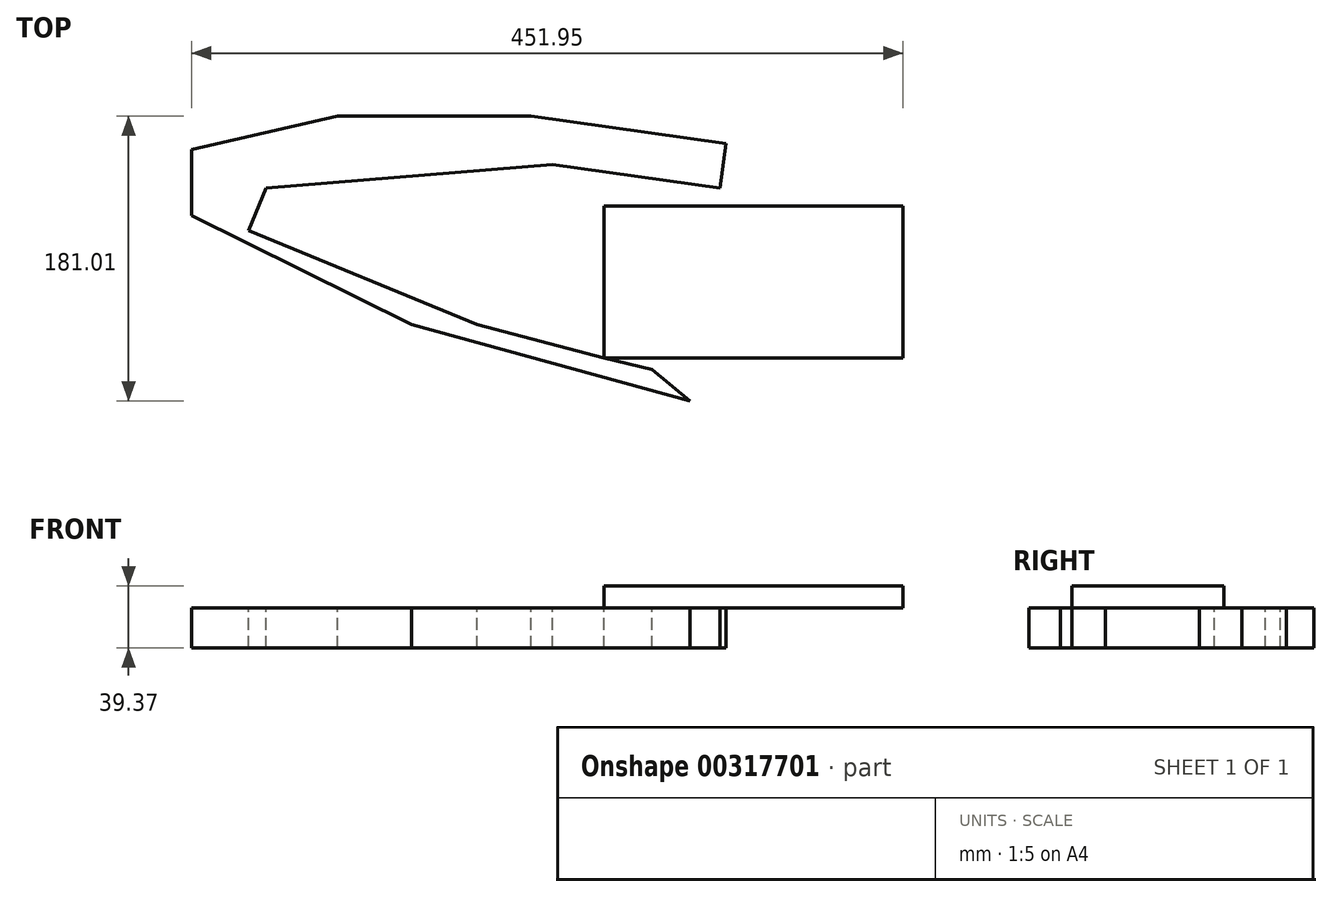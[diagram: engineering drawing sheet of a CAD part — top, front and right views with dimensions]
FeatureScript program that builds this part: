
annotation { "Feature Type Name" : "Feature", "Feature Type Description" : "" }
export const myFeature = defineFeature(function(context is Context, id is Id, definition is map)
    precondition{}
    {
        {
            var Q0;
            Q0=qCreatedBy(makeId("Top.planeOp"),FACE);
            var sketch = newSketch(context, id + "F0", { "sketchPlane" : qUnion([Q0])});
            skLineSegment(sketch, "E0.bottom", {"start": v(74.97, 47.3) * mm, "end": v(-114.93, 47.3) * mm});
            skLineSegment(sketch, "E0.top", {"start": v(74.97, -49.03) * mm, "end": v(-114.93, -49.03) * mm});
            skLineSegment(sketch, "E0.left", {"start": v(74.97, 47.3) * mm, "end": v(74.97, -49.03) * mm});
            skLineSegment(sketch, "E0.right", {"start": v(-114.93, 47.3) * mm, "end": v(-114.93, -49.03) * mm});
            skSolve(sketch);
        }
        {
            var Q0;
            Q0 = qSketchRegion(id + "F0", true);
            extrude(context, id + "F1", {"entities" : qUnion([Q0]), "oppositeDirection" : true, "depth" : 13.97 * mm});
        }
        {
            var Q0;
            Q0=makeQuery(id+"F1.opExtrude","CAP_FACE",FACE,{"disambiguationData":[OSD([sQuery(id+"F0.wireOp",EDGE,"E0.bottom"),sQuery(id+"F0.wireOp",EDGE,"E0.top"),sQuery(id+"F0.wireOp",EDGE,"E0.left"),sQuery(id+"F0.wireOp",EDGE,"E0.right")])],"isStart":false});
            var sketch = newSketch(context, id + "F2", { "sketchPlane" : qUnion([Q0])});
            skLineSegment(sketch, "E1", {"start": v(-114.93, 49.03) * mm, "end": v(-195.47, 27.96) * mm});
            skLineSegment(sketch, "E2", {"start": v(-195.47, 27.96) * mm, "end": v(-340.62, -31.76) * mm});
            skLineSegment(sketch, "E3", {"start": v(-340.62, -31.76) * mm, "end": v(-329.49, -58.84) * mm});
            skLineSegment(sketch, "E4", {"start": v(-329.49, -58.84) * mm, "end": v(-147.65, -73.8) * mm});
            skLineSegment(sketch, "E5", {"start": v(-147.65, -73.8) * mm, "end": v(-41.42, -58.84) * mm});
            skLineSegment(sketch, "E6", {"start": v(-41.42, -58.84) * mm, "end": v(-37.43, -87.13) * mm});
            skLineSegment(sketch, "E7", {"start": v(-37.43, -87.13) * mm, "end": v(-161.25, -104.56) * mm});
            skLineSegment(sketch, "E8", {"start": v(-161.25, -104.56) * mm, "end": v(-284.08, -104.56) * mm});
            skLineSegment(sketch, "E9", {"start": v(-284.08, -104.56) * mm, "end": v(-376.98, -83.15) * mm});
            skLineSegment(sketch, "E10", {"start": v(-376.98, -83.15) * mm, "end": v(-376.98, -41.38) * mm});
            skLineSegment(sketch, "E11", {"start": v(-376.98, -41.38) * mm, "end": v(-237.07, 27.96) * mm});
            skLineSegment(sketch, "E12", {"start": v(-237.07, 27.96) * mm, "end": v(-60.4, 76.45) * mm});
            skLineSegment(sketch, "E13", {"start": v(-60.4, 76.45) * mm, "end": v(-84.59, 56.6) * mm});
            skLineSegment(sketch, "E14", {"start": v(-84.59, 56.6) * mm, "end": v(-114.93, 49.03) * mm});
            skSolve(sketch);
        }
        {
            var Q0;
            Q0 = qSketchRegion(id + "F2", true);
            extrude(context, id + "F3", {"entities" : qUnion([Q0]), "depth" : 25.4 * mm});
        }
    });
